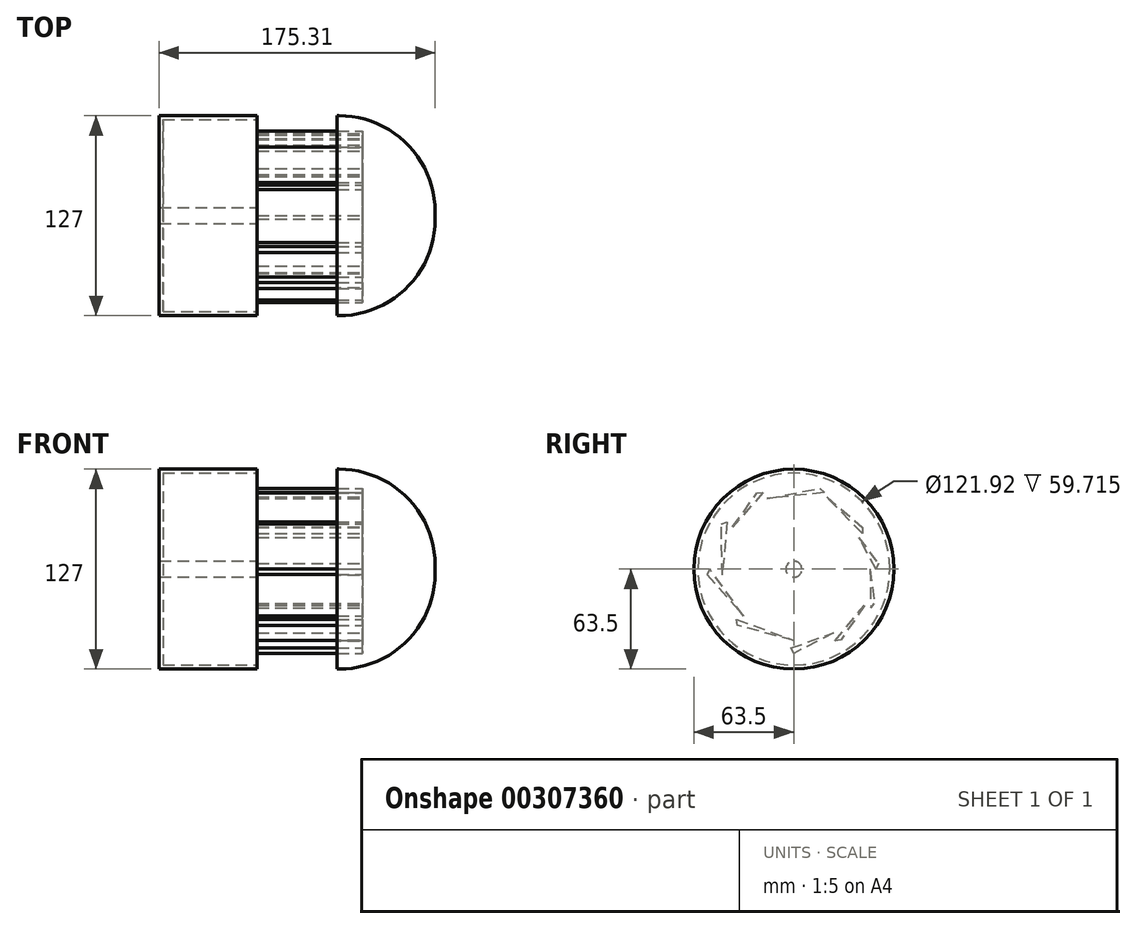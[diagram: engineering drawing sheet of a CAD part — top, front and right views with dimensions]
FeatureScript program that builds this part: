
annotation { "Feature Type Name" : "Feature", "Feature Type Description" : "" }
export const myFeature = defineFeature(function(context is Context, id is Id, definition is map)
    precondition{}
    {
        {
            var Q0;
            Q0=qCreatedBy(makeId("Right.planeOp"),FACE);
            var sketch = newSketch(context, id + "F0", { "sketchPlane" : qUnion([Q0])});
            skCircle(sketch, "E0", {"center": v(0, 0) * mm, "radius": 63.5 * mm});
            skSolve(sketch);
        }
        {
            var Q0;
            Q0=makeQuery(id+"F0.imprint","IMPRINT",FACE,{"disambiguationData":[TD([[makeQuery(id+"F0.imprint","IMPRINT",EDGE,{"derivedFrom":sQuery(id+"F0.wireOp",EDGE,"E0")}),1.0]])]});
            extrude(context, id + "F1", {"entities" : qUnion([Q0]), "depth" : 62.25 * mm});
        }
        {
            var Q0;
            Q0=makeQuery(id+"F1.opExtrude","CAP_FACE",FACE,{"disambiguationData":[OSD([sQuery(id+"F0.wireOp",EDGE,"E0")])],"isStart":false});
            fillet(context, id + "F2", {"entities" : qUnion([Q0]), "radius" : 60.96 * mm, "tangentPropagation" : true, "allowEdgeOverflow" : false});
        }
        {
            var Q0;
            Q0=qCreatedBy(makeId("Right.planeOp"),FACE);
            var sketch = newSketch(context, id + "F3", { "sketchPlane" : qUnion([Q0])});
            skLineSegment(sketch, "E1", {"start": v(0, -53.43) * mm, "end": v(-1.96, -50.16) * mm});
            skLineSegment(sketch, "E2", {"start": v(-1.96, -50.16) * mm, "end": v(25.04, -40.58) * mm});
            skLineSegment(sketch, "E3", {"start": v(25.04, -40.58) * mm, "end": v(0, -53.43) * mm});
            skLineSegment(sketch, "E4", {"start": v(29.82, -44.88) * mm, "end": v(26.07, -45.56) * mm});
            skLineSegment(sketch, "E5", {"start": v(26.07, -45.56) * mm, "end": v(44.9, -23.02) * mm});
            skLineSegment(sketch, "E6", {"start": v(44.9, -23.02) * mm, "end": v(29.82, -44.88) * mm});
            skLineSegment(sketch, "E7", {"start": v(53.7, 3.52) * mm, "end": v(52.26, 0) * mm});
            skLineSegment(sketch, "E8", {"start": v(52.26, 0) * mm, "end": v(41.16, 20.15) * mm});
            skLineSegment(sketch, "E9", {"start": v(41.16, 20.15) * mm, "end": v(53.7, 3.52) * mm});
            skLineSegment(sketch, "E10", {"start": v(43.63, 26.62) * mm, "end": v(43.4, 22.82) * mm});
            skLineSegment(sketch, "E11", {"start": v(43.4, 22.82) * mm, "end": v(21, 45.76) * mm});
            skLineSegment(sketch, "E12", {"start": v(21, 45.76) * mm, "end": v(43.63, 26.62) * mm});
            skLineSegment(sketch, "E13", {"start": v(-16.98, 44.9) * mm, "end": v(16.66, 51.33) * mm});
            skLineSegment(sketch, "E14", {"start": v(48.88, -24.6) * mm, "end": v(51.32, -21.68) * mm});
            skLineSegment(sketch, "E15", {"start": v(48.35, 0) * mm, "end": v(48.88, -24.6) * mm});
            skLineSegment(sketch, "E16", {"start": v(48.35, 0) * mm, "end": v(51.32, -21.68) * mm});
            skLineSegment(sketch, "E17", {"start": v(-23.32, 48.47) * mm, "end": v(-19.51, 48.67) * mm});
            skLineSegment(sketch, "E18", {"start": v(-19.51, 48.67) * mm, "end": v(-38.85, 26.77) * mm});
            skLineSegment(sketch, "E19", {"start": v(-38.85, 26.77) * mm, "end": v(-23.32, 48.47) * mm});
            skLineSegment(sketch, "E20", {"start": v(-46.1, 28.82) * mm, "end": v(-42.46, 29.92) * mm});
            skLineSegment(sketch, "E21", {"start": v(-42.46, 29.92) * mm, "end": v(-45.47, -3.74) * mm});
            skLineSegment(sketch, "E22", {"start": v(-45.47, -3.74) * mm, "end": v(-46.1, 28.82) * mm});
            skLineSegment(sketch, "E23", {"start": v(-53.42, 0) * mm, "end": v(-55.16, -3.3) * mm});
            skLineSegment(sketch, "E24", {"start": v(-55.16, -3.3) * mm, "end": v(-31.95, -29.64) * mm});
            skLineSegment(sketch, "E25", {"start": v(-31.95, -29.64) * mm, "end": v(-53.42, 0) * mm});
            skLineSegment(sketch, "E26", {"start": v(-35.95, -35.68) * mm, "end": v(-36.58, -31.92) * mm});
            skLineSegment(sketch, "E27", {"start": v(-36.58, -31.92) * mm, "end": v(0, -45.28) * mm});
            skLineSegment(sketch, "E28", {"start": v(0, -45.28) * mm, "end": v(-35.95, -35.68) * mm});
            skLineSegment(sketch, "E29", {"start": v(16.66, 51.33) * mm, "end": v(19.4, 48.69) * mm});
            skLineSegment(sketch, "E30", {"start": v(19.4, 48.69) * mm, "end": v(-16.98, 44.9) * mm});
            skSolve(sketch);
        }
        {
            var Q0;
            Q0=qSketchRegion(id+"F3",true);
            extrude(context, id + "F4", {"entities" : qUnion([Q0]), "oppositeDirection" : true, "depth" : 50.8 * mm, "hasSecondDirection" : true, "secondDirectionOppositeDirection" : false, "secondDirectionDepth" : 16.26 * mm});
        }
        {
            var Q0;
            Q0=makeQuery(id+"F4.opExtrude","CAP_FACE",FACE,{"disambiguationData":[OSD([sQuery(id+"F3.wireOp",EDGE,"E20"),sQuery(id+"F3.wireOp",EDGE,"E21"),sQuery(id+"F3.wireOp",EDGE,"E22")])],"isStart":false});
            var sketch = newSketch(context, id + "F5", { "sketchPlane" : qUnion([Q0])});
            skCircle(sketch, "E31", {"center": v(0, 0) * mm, "radius": 63.5 * mm});
            skSolve(sketch);
        }
        {
            var Q0;
            Q0=qSketchRegion(id+"F5",true);
            extrude(context, id + "F6", {"entities" : qUnion([Q0]), "depth" : 62.26 * mm});
        }
        {
            var Q0;
            Q0=makeQuery(id+"F6.opExtrude","CAP_FACE",FACE,{"disambiguationData":[OSD([sQuery(id+"F5.wireOp",EDGE,"E31")])],"isStart":true});
            shell(context, id + "F7", {"entities" : qUnion([Q0]), "thickness" : 2.54 * mm});
        }
        {
            var Q0;
            Q0=makeQuery(id+"F4.opExtrude","CAP_FACE",FACE,{"disambiguationData":[OSD([sQuery(id+"F3.wireOp",EDGE,"E17"),sQuery(id+"F3.wireOp",EDGE,"E18"),sQuery(id+"F3.wireOp",EDGE,"E19")])],"isStart":false});
            var sketch = newSketch(context, id + "F8", { "sketchPlane" : qUnion([Q0])});
            skLineSegment(sketch, "E32", {"start": v(0, 0) * mm, "end": v(29.58, 0) * mm});
            skLineSegment(sketch, "E33", {"start": v(29.58, 0) * mm, "end": v(-29.58, 0) * mm});
            skCircle(sketch, "E34", {"center": v(0, 0) * mm, "radius": 5.08 * mm});
            skSolve(sketch);
        }
        {
            var Q0;
            Q0=qSketchRegion(id+"F8",true);
            extrude(context, id + "F9", {"entities" : qUnion([Q0]), "depth" : 62.1 * mm});
        }
    });
